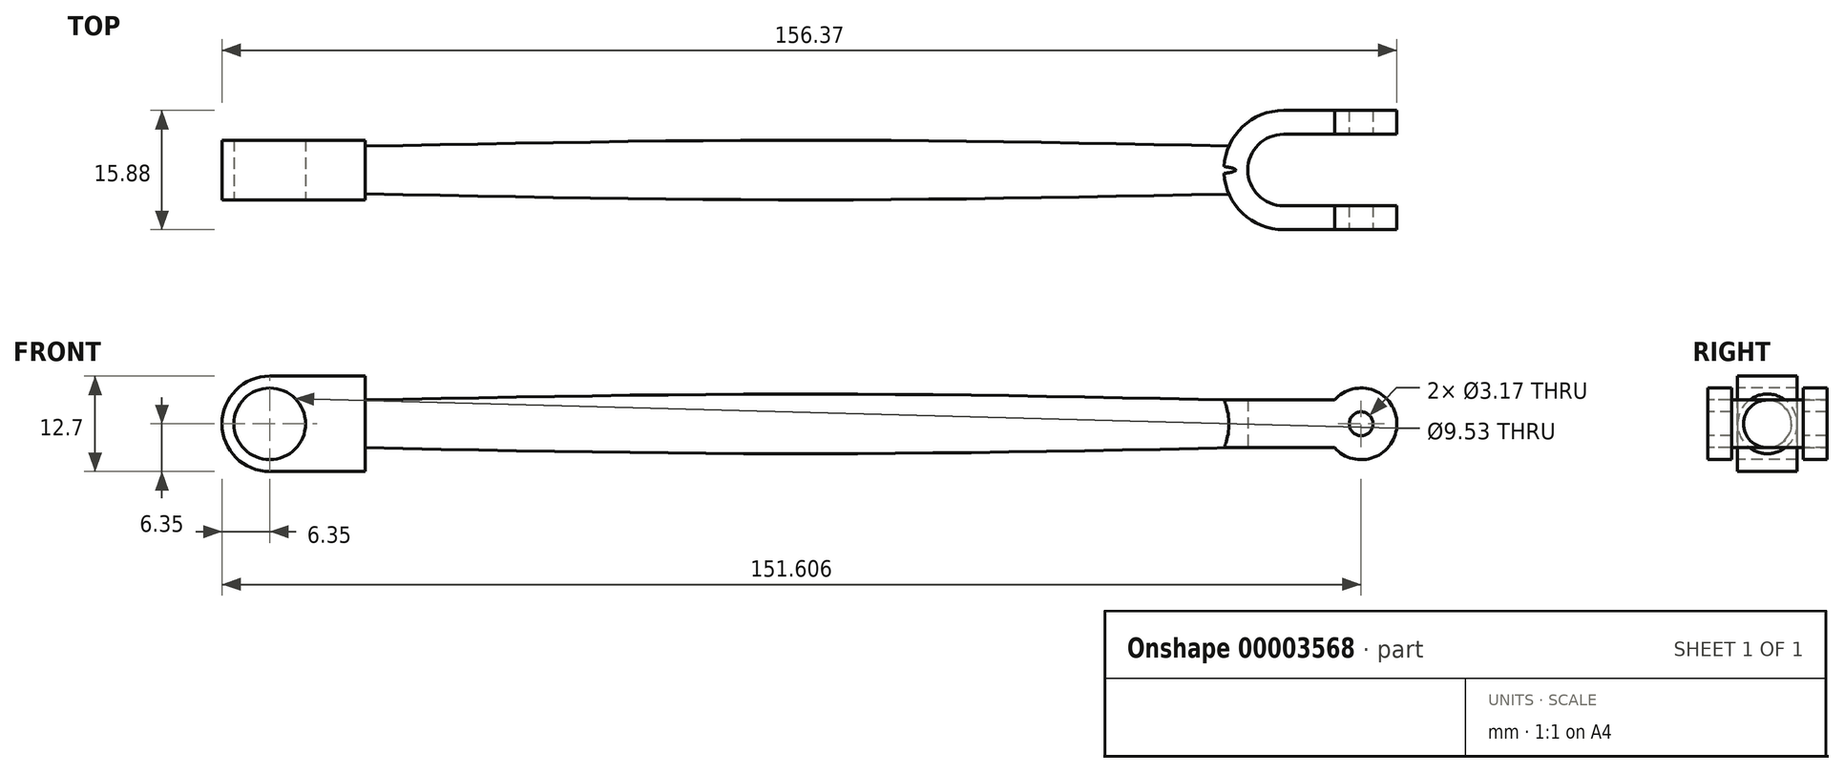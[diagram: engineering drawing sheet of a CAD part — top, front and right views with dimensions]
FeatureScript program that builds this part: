
annotation { "Feature Type Name" : "Feature", "Feature Type Description" : "" }
export const myFeature = defineFeature(function(context is Context, id is Id, definition is map)
    precondition{}
    {
        {
            var Q0;
            Q0=qCreatedBy(makeId("Front.planeOp"),FACE);
            var sketch = newSketch(context, id + "F0", { "sketchPlane" : qUnion([Q0])});
            skArc(sketch, "E0", {"start": v(0, 6.35) * mm, "mid": v(-6.35, 0) * mm, "end": v(0, -6.35) * mm});
            skLineSegment(sketch, "E1.bottom", {"start": v(0, 6.35) * mm, "end": v(12.7, 6.35) * mm});
            skLineSegment(sketch, "E1.top", {"start": v(0, -6.35) * mm, "end": v(12.7, -6.35) * mm});
            skLineSegment(sketch, "E1.right", {"start": v(12.7, 6.35) * mm, "end": v(12.7, -6.35) * mm});
            skSolve(sketch);
        }
        {
            var Q0;
            Q0 = qSketchRegion(id + "F0", true);
            extrude(context, id + "F1", {"entities" : qUnion([Q0]), "depth" : 7.94 * mm});
        }
        {
            var Q0;
            Q0=makeQuery(id+"F1.opExtrude","CAP_FACE",FACE,{"disambiguationData":[OSD([sQuery(id+"F0.wireOp",EDGE,"E0"),sQuery(id+"F0.wireOp",EDGE,"E1.bottom"),sQuery(id+"F0.wireOp",EDGE,"E1.top"),sQuery(id+"F0.wireOp",EDGE,"E1.right")])],"isStart":false});
            var sketch = newSketch(context, id + "F2", { "sketchPlane" : qUnion([Q0])});
            skCircle(sketch, "E2", {"center": v(0, 0) * mm, "radius": 4.76 * mm});
            skSolve(sketch);
        }
        {
            var Q0;
            Q0 = qSketchRegion(id + "F2", true);
            extrude(context, id + "F3", {"entities" : qUnion([Q0]), "operationType" : NewBodyOperationType.REMOVE, "oppositeDirection" : true, "depth" : 25.4 * mm});
        }
        {
            var Q0;
            Q0=qCreatedBy(makeId("Front.planeOp"),FACE);
            var Q1;
            Q1=makeQuery(id+"F1.opExtrude","CAP_FACE",FACE,{"disambiguationData":[OSD([sQuery(id+"F0.wireOp",EDGE,"E0"),sQuery(id+"F0.wireOp",EDGE,"E1.bottom"),sQuery(id+"F0.wireOp",EDGE,"E1.top"),sQuery(id+"F0.wireOp",EDGE,"E1.right")])],"isStart":false});
            cPlane(context, id + "F4", {"entities" : qUnion([Q0, Q1]), "cplaneType" : CPlaneType.MID_PLANE, "offset" : 152.4 * mm, "width" : 152.4 * mm, "height" : 152.4 * mm});
        }
        {
            var Q0;
            Q0=qCreatedBy(id+"F4.planeOp",FACE);
            var sketch = newSketch(context, id + "F5", { "sketchPlane" : qUnion([Q0])});
            skLineSegment(sketch, "E3", {"start": v(0, 0) * mm, "end": v(153.2, 0) * mm, "construction": true});
            skLineSegment(sketch, "E4", {"start": v(12.7, 3.97) * mm, "end": v(134.94, 3.97) * mm, "construction": true});
            skLineSegment(sketch, "E5", {"start": v(73.82, 3.97) * mm, "end": v(73.82, 0) * mm, "construction": true});
            skLineSegment(sketch, "E6", {"start": v(134.94, 3.97) * mm, "end": v(134.94, 0) * mm, "construction": true});
            skSolve(sketch);
        }
        {
            var Q0;
            Q0=qCreatedBy(makeId("Top.planeOp"),FACE);
            var sketch = newSketch(context, id + "F6", { "sketchPlane" : qUnion([Q0])});
            skArc(sketch, "E7", {"start": v(134.94, 3.97) * mm, "mid": v(127, -3.97) * mm, "end": v(134.94, -11.9) * mm});
            skLineSegment(sketch, "E8", {"start": v(134.94, 3.97) * mm, "end": v(145.26, 3.97) * mm});
            skLineSegment(sketch, "E9", {"start": v(145.26, 3.97) * mm, "end": v(145.26, 0.8) * mm});
            skLineSegment(sketch, "E10", {"start": v(145.26, 0.8) * mm, "end": v(134.94, 0.8) * mm});
            skLineSegment(sketch, "E11", {"start": v(134.94, -11.9) * mm, "end": v(145.26, -11.9) * mm});
            skLineSegment(sketch, "E12", {"start": v(145.26, -11.9) * mm, "end": v(145.26, -8.73) * mm});
            skLineSegment(sketch, "E13", {"start": v(145.26, -8.73) * mm, "end": v(134.94, -8.73) * mm});
            skArc(sketch, "E14", {"start": v(134.94, 0.8) * mm, "mid": v(130.18, -3.97) * mm, "end": v(134.94, -8.73) * mm});
            skSolve(sketch);
        }
        {
            var Q0;
            Q0=makeQuery(id+"F1.opExtrude","SWEPT_FACE",FACE,{"disambiguationData":[OSD([sQuery(id+"F0.wireOp",EDGE,"E1.right")])]});
            var sketch = newSketch(context, id + "F7", { "sketchPlane" : qUnion([Q0])});
            skCircle(sketch, "E15", {"center": v(-3.97, 0) * mm, "radius": 3.18 * mm});
            skSolve(sketch);
        }
        {
            var Q0;
            Q0=sQuery(id+"F5.wireOp",EDGE,"E5");
            cPlane(context, id + "F8", {"entities" : qUnion([Q0]), "cplaneType" : CPlaneType.LINE_ANGLE, "offset" : 152.4 * mm, "angle" : 0 * degree, "width" : 152.4 * mm, "height" : 152.4 * mm});
        }
        {
            var Q0;
            Q0=qCreatedBy(id+"F8.planeOp",FACE);
            var sketch = newSketch(context, id + "F9", { "sketchPlane" : qUnion([Q0])});
            skCircle(sketch, "E16", {"center": v(3.97, 0) * mm, "radius": 3.97 * mm});
            skSolve(sketch);
        }
        {
            var Q0;
            Q0=sQuery(id+"F5.wireOp",EDGE,"E6");
            cPlane(context, id + "F10", {"entities" : qUnion([Q0]), "cplaneType" : CPlaneType.LINE_ANGLE, "offset" : 152.4 * mm, "angle" : 0 * degree, "width" : 152.4 * mm, "height" : 152.4 * mm});
        }
        {
            var Q0;
            Q0=qCreatedBy(id+"F10.planeOp",FACE);
            cPlane(context, id + "F11", {"entities" : qUnion([Q0]), "cplaneType" : CPlaneType.OFFSET, "offset" : 6.35 * mm, "width" : 152.4 * mm, "height" : 152.4 * mm});
        }
        {
            var Q0;
            Q0=qCreatedBy(id+"F11.planeOp",FACE);
            var sketch = newSketch(context, id + "F12", { "sketchPlane" : qUnion([Q0])});
            skCircle(sketch, "E17", {"center": v(3.97, 0) * mm, "radius": 3.18 * mm});
            skSolve(sketch);
        }
        {
            var Q1;
            Q1=makeQuery(id+"F7.imprint","IMPRINT",FACE,{"disambiguationData":[TD([[makeQuery(id+"F7.imprint","IMPRINT",EDGE,{"derivedFrom":sQuery(id+"F7.wireOp",EDGE,"E15")}),1.0]])]});
            var Q2;
            Q2=makeQuery(id+"F9.imprint","IMPRINT",FACE,{"disambiguationData":[TD([[makeQuery(id+"F9.imprint","IMPRINT",EDGE,{"derivedFrom":sQuery(id+"F9.wireOp",EDGE,"E16")}),1.0]])]});
            var Q3;
            Q3=makeQuery(id+"F12.imprint","IMPRINT",FACE,{"disambiguationData":[TD([[makeQuery(id+"F12.imprint","IMPRINT",EDGE,{"derivedFrom":sQuery(id+"F12.wireOp",EDGE,"E17")}),1.0]])]});
            loft(context, id + "F13", {"operationType" : NewBodyOperationType.ADD, "sheetProfilesArray" : [{ "sheetProfileEntities" : qUnion([Q1]) }, { "sheetProfileEntities" : qUnion([Q2]) }, { "sheetProfileEntities" : qUnion([Q3]) }]});
        }
        {
            var Q0;
            Q0=makeQuery(id+"F6.imprint","IMPRINT",FACE,{"disambiguationData":[TD([[makeQuery(id+"F6.imprint","IMPRINT",EDGE,{"derivedFrom":sQuery(id+"F6.wireOp",EDGE,"E7")}),1.0]])]});
            extrude(context, id + "F14", {"entities" : qUnion([Q0]), "operationType" : NewBodyOperationType.ADD, "depth" : 3.17 * mm, "hasSecondDirection" : true, "secondDirectionOppositeDirection" : true, "secondDirectionDepth" : 3.17 * mm});
        }
        {
            var Q0;
            Q0=makeQuery(id+"F14.opExtrude","SWEPT_FACE",FACE,{"disambiguationData":[OSD([sQuery(id+"F6.wireOp",EDGE,"E11")])]});
            var sketch = newSketch(context, id + "F15", { "sketchPlane" : qUnion([Q0])});
            skCircle(sketch, "E18", {"center": v(145.26, 0) * mm, "radius": 4.76 * mm});
            skSolve(sketch);
        }
        {
            var Q0;
            Q0 = qSketchRegion(id + "F15", true);
            var Q1;
            Q1=makeQuery(id+"F14.opExtrude","SWEPT_FACE",FACE,{"disambiguationData":[OSD([sQuery(id+"F6.wireOp",EDGE,"E13")])]});
            extrude(context, id + "F16", {"entities" : qUnion([Q0]), "operationType" : NewBodyOperationType.ADD, "endBound" : BoundingType.UP_TO_SURFACE, "oppositeDirection" : true, "endBoundEntityFace" : qUnion([Q1]), "depth" : 25.4 * mm});
        }
        {
            var Q0;
            Q0=makeQuery(id+"F14.opExtrude","SWEPT_FACE",FACE,{"disambiguationData":[OSD([sQuery(id+"F6.wireOp",EDGE,"E8")])]});
            var sketch = newSketch(context, id + "F17", { "sketchPlane" : qUnion([Q0])});
            skCircle(sketch, "E19", {"center": v(-145.26, 0) * mm, "radius": 4.76 * mm});
            skSolve(sketch);
        }
        {
            var Q0;
            Q0 = qSketchRegion(id + "F17", true);
            var Q1;
            Q1=makeQuery(id+"F14.opExtrude","SWEPT_FACE",FACE,{"disambiguationData":[OSD([sQuery(id+"F6.wireOp",EDGE,"E10")])]});
            extrude(context, id + "F18", {"entities" : qUnion([Q0]), "operationType" : NewBodyOperationType.ADD, "endBound" : BoundingType.UP_TO_SURFACE, "oppositeDirection" : true, "endBoundEntityFace" : qUnion([Q1]), "depth" : 25.4 * mm});
        }
        {
            var Q0;
            Q0=makeQuery(id+"F16.boolean.opBoolean","MERGE",FACE,{"derivedFrom":[makeQuery(id+"F14.opExtrude","SWEPT_FACE",FACE,{"disambiguationData":[OSD([sQuery(id+"F6.wireOp",EDGE,"E11")])]}),makeQuery(id+"F16.opExtrude","CAP_FACE",FACE,{"disambiguationData":[OSD([sQuery(id+"F15.wireOp",EDGE,"E18")])],"isStart":true})]});
            var sketch = newSketch(context, id + "F19", { "sketchPlane" : qUnion([Q0])});
            skCircle(sketch, "E20", {"center": v(145.26, 0) * mm, "radius": 1.59 * mm});
            skSolve(sketch);
        }
        {
            var Q0;
            Q0 = qSketchRegion(id + "F19", true);
            extrude(context, id + "F20", {"entities" : qUnion([Q0]), "operationType" : NewBodyOperationType.REMOVE, "endBound" : BoundingType.THROUGH_ALL, "oppositeDirection" : true, "depth" : 25.4 * mm});
        }
    });
